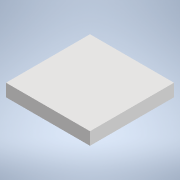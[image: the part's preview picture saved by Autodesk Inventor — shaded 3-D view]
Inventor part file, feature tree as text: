
AUTODESK INVENTOR PART (.ipt)
format: ipt  version: 2022 (Build 260153000, 153)  size: 88,576 bytes
history: native  units: mm
features: other x1, extrude x1, sketch x1
ambient origin geometry x8: Origin, YZ Plane, XZ Plane, XY Plane, X Axis, Y Axis, Z Axis, Center Point
bodies: Body1 (feature_tree)
feature tree (3):
  other  "Твердое тело1"
  extrude  "Выдавливание1"  Depth=40.0mm
  sketch  "Эскиз1"
